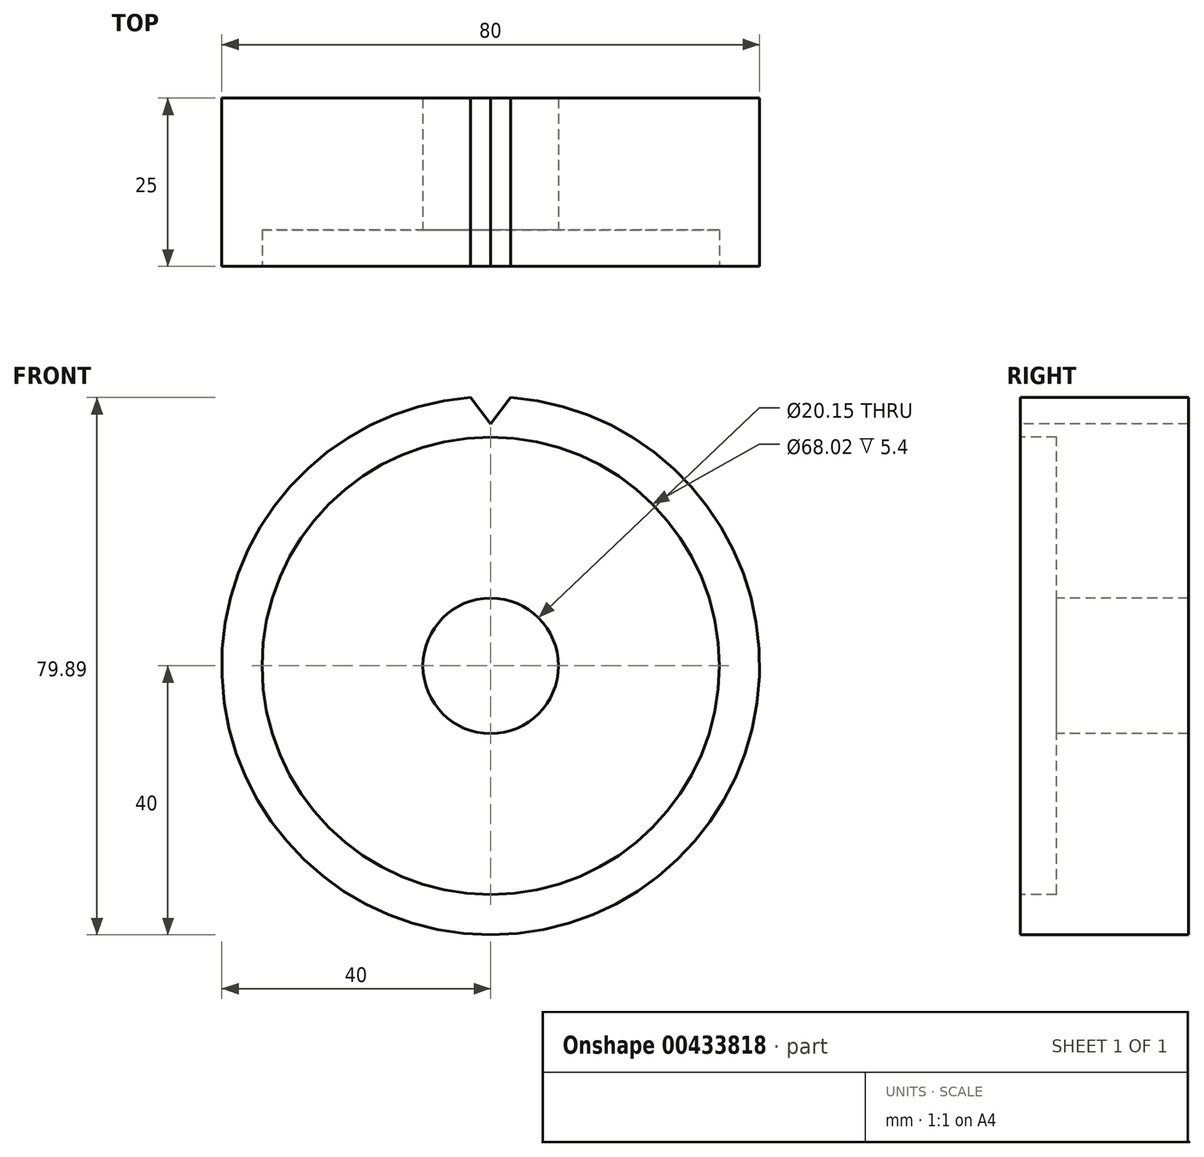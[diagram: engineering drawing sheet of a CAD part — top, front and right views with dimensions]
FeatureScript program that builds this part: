
annotation { "Feature Type Name" : "Feature", "Feature Type Description" : "" }
export const myFeature = defineFeature(function(context is Context, id is Id, definition is map)
    precondition{}
    {
        {
            var Q0;
            Q0=qCreatedBy(makeId("Front.planeOp"),FACE);
            var sketch = newSketch(context, id + "F0", { "sketchPlane" : qUnion([Q0])});
            skCircle(sketch, "E0", {"center": v(0, 0) * mm, "radius": 40 * mm});
            skSolve(sketch);
        }
        {
            var Q0;
            Q0 = qSketchRegion(id + "F0", true);
            extrude(context, id + "F1", {"entities" : qUnion([Q0]), "depth" : 25 * mm});
        }
        {
            var Q0;
            Q0=makeQuery(id+"F1.opExtrude","CAP_FACE",FACE,{"disambiguationData":[OSD([sQuery(id+"F0.wireOp",EDGE,"E0")])],"isStart":false});
            var sketch = newSketch(context, id + "F2", { "sketchPlane" : qUnion([Q0])});
            skCircle(sketch, "E1.0.0", {"center": v(0, 0) * mm, "radius": 40 * mm});
            skLineSegment(sketch, "E2", {"start": v(0, 0) * mm, "end": v(0, 43.2) * mm});
            skLineSegment(sketch, "E3", {"start": v(-3, 39.89) * mm, "end": v(0, 36) * mm});
            skLineSegment(sketch, "E4", {"start": v(0, 36) * mm, "end": v(3, 39.89) * mm});
            skSolve(sketch);
        }
        {
            var Q0;
            {var subQ0=sQuery(id+"F2.wireOp",EDGE,"E3");Q0=makeQuery(id+"F2.imprint","IMPRINT",FACE,{"disambiguationData":[TD([[makeQuery(id+"F2.imprint","IMPRINT",EDGE,{"derivedFrom":subQ0}),1.0]])]});}
            var Q1;
            {var subQ0=sQuery(id+"F2.wireOp",EDGE,"E4");Q1=makeQuery(id+"F2.imprint","IMPRINT",FACE,{"disambiguationData":[TD([[makeQuery(id+"F2.imprint","IMPRINT",EDGE,{"derivedFrom":subQ0}),1.0]])]});}
            extrude(context, id + "F3", {"entities" : qUnion([Q0, Q1]), "operationType" : NewBodyOperationType.REMOVE, "oppositeDirection" : true, "depth" : 25 * mm});
        }
        {
            var Q0;
            {var subQ0=sQuery(id+"F2.wireOp",EDGE,"E3");Q0=makeQuery(id+"F2.imprint","IMPRINT",FACE,{"disambiguationData":[TD([[makeQuery(id+"F2.imprint","IMPRINT",EDGE,{"derivedFrom":subQ0}),-1.0]])]});}
            var sketch = newSketch(context, id + "F4", { "sketchPlane" : qUnion([Q0])});
            skCircle(sketch, "E5", {"center": v(0, 0) * mm, "radius": 10.08 * mm});
            skSolve(sketch);
        }
        {
            var Q0;
            Q0 = qSketchRegion(id + "F4", true);
            extrude(context, id + "F5", {"entities" : qUnion([Q0]), "operationType" : NewBodyOperationType.REMOVE, "oppositeDirection" : true, "depth" : 25 * mm});
        }
        {
            var Q0;
            {var subQ0=sQuery(id+"F2.wireOp",EDGE,"E3");Q0=makeQuery(id+"F2.imprint","IMPRINT",FACE,{"disambiguationData":[TD([[makeQuery(id+"F2.imprint","IMPRINT",EDGE,{"derivedFrom":subQ0}),-1.0]])]});}
            var sketch = newSketch(context, id + "F6", { "sketchPlane" : qUnion([Q0])});
            skCircle(sketch, "E6", {"center": v(0, 0) * mm, "radius": 34 * mm});
            skSolve(sketch);
        }
        {
            var Q0;
            Q0=makeQuery(id+"F6.imprint","IMPRINT",FACE,{"disambiguationData":[TD([[makeQuery(id+"F6.imprint","IMPRINT",EDGE,{"derivedFrom":sQuery(id+"F6.wireOp",EDGE,"E6")}),1.0]])]});
            extrude(context, id + "F7", {"entities" : qUnion([Q0]), "operationType" : NewBodyOperationType.REMOVE, "oppositeDirection" : true, "depth" : 5.4 * mm});
        }
    });
